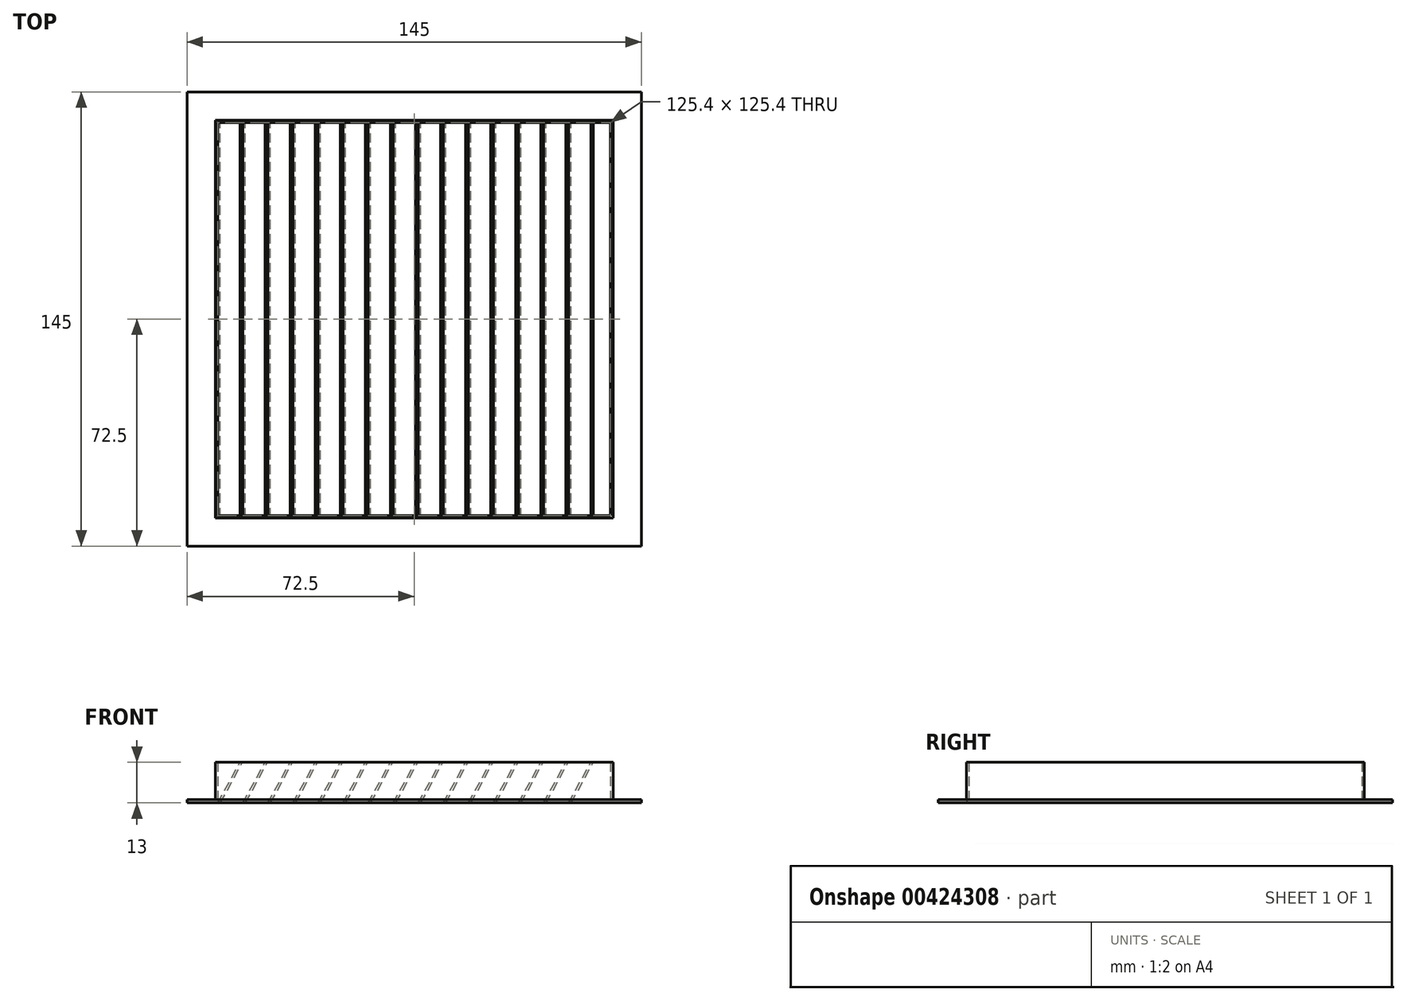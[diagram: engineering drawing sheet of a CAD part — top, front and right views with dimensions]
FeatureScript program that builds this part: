
annotation { "Feature Type Name" : "Feature", "Feature Type Description" : "" }
export const myFeature = defineFeature(function(context is Context, id is Id, definition is map)
    precondition{}
    {
        {
            var Q0;
            Q0=qCreatedBy(makeId("Top.planeOp"),FACE);
            var sketch = newSketch(context, id + "F0", { "sketchPlane" : qUnion([Q0])});
            skLineSegment(sketch, "E0.bottom", {"start": v(63.5, -63.5) * mm, "end": v(-63.5, -63.5) * mm});
            skLineSegment(sketch, "E0.top", {"start": v(63.5, 63.5) * mm, "end": v(-63.5, 63.5) * mm});
            skLineSegment(sketch, "E0.left", {"start": v(63.5, -63.5) * mm, "end": v(63.5, 63.5) * mm});
            skLineSegment(sketch, "E0.right", {"start": v(-63.5, -63.5) * mm, "end": v(-63.5, 63.5) * mm});
            skPoint(sketch, "E0.middle", {"position": v(0, 0) * mm});
            skLineSegment(sketch, "E1.0", {"start": v(62.7, 62.7) * mm, "end": v(-62.7, 62.7) * mm});
            skLineSegment(sketch, "E1.1", {"start": v(62.7, -62.7) * mm, "end": v(62.7, 62.7) * mm});
            skLineSegment(sketch, "E1.2", {"start": v(62.7, -62.7) * mm, "end": v(-62.7, -62.7) * mm});
            skLineSegment(sketch, "E1.3", {"start": v(-62.7, -62.7) * mm, "end": v(-62.7, 62.7) * mm});
            skLineSegment(sketch, "E2.bottom", {"start": v(72.5, -72.5) * mm, "end": v(-72.5, -72.5) * mm});
            skLineSegment(sketch, "E2.top", {"start": v(72.5, 72.5) * mm, "end": v(-72.5, 72.5) * mm});
            skLineSegment(sketch, "E2.left", {"start": v(72.5, -72.5) * mm, "end": v(72.5, 72.5) * mm});
            skLineSegment(sketch, "E2.right", {"start": v(-72.5, -72.5) * mm, "end": v(-72.5, 72.5) * mm});
            skSolve(sketch);
        }
        {
            var Q0;
            Q0=makeQuery(id+"F0.imprint","IMPRINT",FACE,{"disambiguationData":[TD([[makeQuery(id+"F0.imprint","IMPRINT",EDGE,{"derivedFrom":sQuery(id+"F0.wireOp",EDGE,"E0.bottom")}),1.0]])]});
            var Q1;
            Q1=makeQuery(id+"F0.imprint","IMPRINT",FACE,{"disambiguationData":[TD([[makeQuery(id+"F0.imprint","IMPRINT",EDGE,{"derivedFrom":sQuery(id+"F0.wireOp",EDGE,"E0.bottom")}),-1.0]])]});
            extrude(context, id + "F1", {"entities" : qUnion([Q0, Q1]), "depth" : 1 * mm});
        }
        {
            var Q0;
            Q0=makeQuery(id+"F0.imprint","IMPRINT",FACE,{"disambiguationData":[TD([[makeQuery(id+"F0.imprint","IMPRINT",EDGE,{"derivedFrom":sQuery(id+"F0.wireOp",EDGE,"E0.bottom")}),-1.0]])]});
            extrude(context, id + "F2", {"entities" : qUnion([Q0]), "operationType" : NewBodyOperationType.ADD, "depth" : 13 * mm});
        }
        {
            var Q0;
            {var subQ0=sQuery(id+"F0.wireOp",EDGE,"E1.0");Q0=makeQuery(id+"F2.boolean.opBoolean","MERGE",FACE,{"derivedFrom":[makeQuery(id+"F1.opExtrude","SWEPT_FACE",FACE,{"disambiguationData":[OSD([subQ0])]}),makeQuery(id+"F2.opExtrude","SWEPT_FACE",FACE,{"disambiguationData":[OSD([subQ0])]})]});}
            var sketch = newSketch(context, id + "F3", { "sketchPlane" : qUnion([Q0])});
            skLineSegment(sketch, "E3", {"start": v(-62.7, 0) * mm, "end": v(-55.61, 13) * mm});
            skLineSegment(sketch, "E4", {"start": v(-61.9, 0) * mm, "end": v(-54.81, 13) * mm});
            skLineSegment(sketch, "E5.1.0.0", {"start": v(-54.7, 0) * mm, "end": v(-47.61, 13) * mm});
            skLineSegment(sketch, "E5.1.0.1", {"start": v(-53.9, 0) * mm, "end": v(-46.81, 13) * mm});
            skLineSegment(sketch, "E5.2.0.0", {"start": v(-46.7, 0) * mm, "end": v(-39.61, 13) * mm});
            skLineSegment(sketch, "E5.2.0.1", {"start": v(-45.9, 0) * mm, "end": v(-38.81, 13) * mm});
            skLineSegment(sketch, "E5.3.0.0", {"start": v(-38.7, 0) * mm, "end": v(-31.61, 13) * mm});
            skLineSegment(sketch, "E5.3.0.1", {"start": v(-37.9, 0) * mm, "end": v(-30.81, 13) * mm});
            skLineSegment(sketch, "E5.4.0.0", {"start": v(-30.7, 0) * mm, "end": v(-23.61, 13) * mm});
            skLineSegment(sketch, "E5.4.0.1", {"start": v(-29.9, 0) * mm, "end": v(-22.81, 13) * mm});
            skLineSegment(sketch, "E5.5.0.0", {"start": v(-22.7, 0) * mm, "end": v(-15.61, 13) * mm});
            skLineSegment(sketch, "E5.5.0.1", {"start": v(-21.9, 0) * mm, "end": v(-14.81, 13) * mm});
            skLineSegment(sketch, "E5.6.0.0", {"start": v(-14.7, 0) * mm, "end": v(-7.61, 13) * mm});
            skLineSegment(sketch, "E5.6.0.1", {"start": v(-13.9, 0) * mm, "end": v(-6.81, 13) * mm});
            skLineSegment(sketch, "E5.7.0.0", {"start": v(-6.7, 0) * mm, "end": v(0.39, 13) * mm});
            skLineSegment(sketch, "E5.7.0.1", {"start": v(-5.9, 0) * mm, "end": v(1.19, 13) * mm});
            skLineSegment(sketch, "E5.8.0.0", {"start": v(1.3, 0) * mm, "end": v(8.39, 13) * mm});
            skLineSegment(sketch, "E5.8.0.1", {"start": v(2.1, 0) * mm, "end": v(9.19, 13) * mm});
            skLineSegment(sketch, "E5.9.0.0", {"start": v(9.3, 0) * mm, "end": v(16.39, 13) * mm});
            skLineSegment(sketch, "E5.9.0.1", {"start": v(10.1, 0) * mm, "end": v(17.19, 13) * mm});
            skLineSegment(sketch, "E5.10.0.0", {"start": v(17.3, 0) * mm, "end": v(24.39, 13) * mm});
            skLineSegment(sketch, "E5.10.0.1", {"start": v(18.1, 0) * mm, "end": v(25.19, 13) * mm});
            skLineSegment(sketch, "E5.11.0.0", {"start": v(25.3, 0) * mm, "end": v(32.39, 13) * mm});
            skLineSegment(sketch, "E5.11.0.1", {"start": v(26.1, 0) * mm, "end": v(33.19, 13) * mm});
            skLineSegment(sketch, "E5.12.0.0", {"start": v(33.3, 0) * mm, "end": v(40.39, 13) * mm});
            skLineSegment(sketch, "E5.12.0.1", {"start": v(34.1, 0) * mm, "end": v(41.19, 13) * mm});
            skLineSegment(sketch, "E5.13.0.0", {"start": v(41.3, 0) * mm, "end": v(48.39, 13) * mm});
            skLineSegment(sketch, "E5.13.0.1", {"start": v(42.1, 0) * mm, "end": v(49.19, 13) * mm});
            skLineSegment(sketch, "E5.14.0.0", {"start": v(49.3, 0) * mm, "end": v(56.39, 13) * mm});
            skLineSegment(sketch, "E5.14.0.1", {"start": v(50.1, 0) * mm, "end": v(57.19, 13) * mm});
            skLineSegment(sketch, "E5.direction1", {"start": v(-62.7, 0) * mm, "end": v(-54.7, 0) * mm, "construction": true});
            skSolve(sketch);
        }
        {
            var Q0;
            {var subQ0=sQuery(id+"F3.wireOp",EDGE,"E3");Q0=makeQuery(id+"F3.imprint","IMPRINT",FACE,{"disambiguationData":[TD([[makeQuery(id+"F3.imprint","IMPRINT",EDGE,{"derivedFrom":subQ0}),-1.0]])]});}
            var Q1;
            {var subQ0=sQuery(id+"F3.wireOp",EDGE,"E5.1.0.0");Q1=makeQuery(id+"F3.imprint","IMPRINT",FACE,{"disambiguationData":[TD([[makeQuery(id+"F3.imprint","IMPRINT",EDGE,{"derivedFrom":subQ0}),-1.0]])]});}
            var Q2;
            {var subQ0=sQuery(id+"F3.wireOp",EDGE,"E5.2.0.0");Q2=makeQuery(id+"F3.imprint","IMPRINT",FACE,{"disambiguationData":[TD([[makeQuery(id+"F3.imprint","IMPRINT",EDGE,{"derivedFrom":subQ0}),-1.0]])]});}
            var Q3;
            {var subQ0=sQuery(id+"F3.wireOp",EDGE,"E5.3.0.0");Q3=makeQuery(id+"F3.imprint","IMPRINT",FACE,{"disambiguationData":[TD([[makeQuery(id+"F3.imprint","IMPRINT",EDGE,{"derivedFrom":subQ0}),-1.0]])]});}
            var Q4;
            {var subQ0=sQuery(id+"F3.wireOp",EDGE,"E5.4.0.0");Q4=makeQuery(id+"F3.imprint","IMPRINT",FACE,{"disambiguationData":[TD([[makeQuery(id+"F3.imprint","IMPRINT",EDGE,{"derivedFrom":subQ0}),-1.0]])]});}
            var Q5;
            {var subQ0=sQuery(id+"F3.wireOp",EDGE,"E5.5.0.0");Q5=makeQuery(id+"F3.imprint","IMPRINT",FACE,{"disambiguationData":[TD([[makeQuery(id+"F3.imprint","IMPRINT",EDGE,{"derivedFrom":subQ0}),-1.0]])]});}
            var Q6;
            {var subQ0=sQuery(id+"F3.wireOp",EDGE,"E5.6.0.0");Q6=makeQuery(id+"F3.imprint","IMPRINT",FACE,{"disambiguationData":[TD([[makeQuery(id+"F3.imprint","IMPRINT",EDGE,{"derivedFrom":subQ0}),-1.0]])]});}
            var Q7;
            {var subQ0=sQuery(id+"F3.wireOp",EDGE,"E5.7.0.0");Q7=makeQuery(id+"F3.imprint","IMPRINT",FACE,{"disambiguationData":[TD([[makeQuery(id+"F3.imprint","IMPRINT",EDGE,{"derivedFrom":subQ0}),-1.0]])]});}
            var Q8;
            {var subQ0=sQuery(id+"F3.wireOp",EDGE,"E5.8.0.0");Q8=makeQuery(id+"F3.imprint","IMPRINT",FACE,{"disambiguationData":[TD([[makeQuery(id+"F3.imprint","IMPRINT",EDGE,{"derivedFrom":subQ0}),-1.0]])]});}
            var Q9;
            {var subQ0=sQuery(id+"F3.wireOp",EDGE,"E5.9.0.0");Q9=makeQuery(id+"F3.imprint","IMPRINT",FACE,{"disambiguationData":[TD([[makeQuery(id+"F3.imprint","IMPRINT",EDGE,{"derivedFrom":subQ0}),-1.0]])]});}
            var Q10;
            {var subQ0=sQuery(id+"F3.wireOp",EDGE,"E5.10.0.0");Q10=makeQuery(id+"F3.imprint","IMPRINT",FACE,{"disambiguationData":[TD([[makeQuery(id+"F3.imprint","IMPRINT",EDGE,{"derivedFrom":subQ0}),-1.0]])]});}
            var Q11;
            {var subQ0=sQuery(id+"F3.wireOp",EDGE,"E5.11.0.0");Q11=makeQuery(id+"F3.imprint","IMPRINT",FACE,{"disambiguationData":[TD([[makeQuery(id+"F3.imprint","IMPRINT",EDGE,{"derivedFrom":subQ0}),-1.0]])]});}
            var Q12;
            {var subQ0=sQuery(id+"F3.wireOp",EDGE,"E5.12.0.0");Q12=makeQuery(id+"F3.imprint","IMPRINT",FACE,{"disambiguationData":[TD([[makeQuery(id+"F3.imprint","IMPRINT",EDGE,{"derivedFrom":subQ0}),-1.0]])]});}
            var Q13;
            {var subQ0=sQuery(id+"F3.wireOp",EDGE,"E5.13.0.0");Q13=makeQuery(id+"F3.imprint","IMPRINT",FACE,{"disambiguationData":[TD([[makeQuery(id+"F3.imprint","IMPRINT",EDGE,{"derivedFrom":subQ0}),-1.0]])]});}
            var Q14;
            {var subQ0=sQuery(id+"F3.wireOp",EDGE,"E5.14.0.0");Q14=makeQuery(id+"F3.imprint","IMPRINT",FACE,{"disambiguationData":[TD([[makeQuery(id+"F3.imprint","IMPRINT",EDGE,{"derivedFrom":subQ0}),-1.0]])]});}
            var Q15;
            {var subQ0=sQuery(id+"F3.wireOp",EDGE,"524b8a1f-dfb2-4648-83e8-d59a4865afdb.0.15.0");Q15=makeQuery(id+"F3.imprint","IMPRINT",FACE,{"disambiguationData":[TD([[makeQuery(id+"F3.imprint","IMPRINT",EDGE,{"derivedFrom":subQ0}),-1.0]])]});}
            var Q16;
            {var subQ0=sQuery(id+"F3.wireOp",EDGE,"524b8a1f-dfb2-4648-83e8-d59a4865afdb.0.16.0");Q16=makeQuery(id+"F3.imprint","IMPRINT",FACE,{"disambiguationData":[TD([[makeQuery(id+"F3.imprint","IMPRINT",EDGE,{"derivedFrom":subQ0}),-1.0]])]});}
            var Q17;
            {var subQ0=sQuery(id+"F3.wireOp",EDGE,"524b8a1f-dfb2-4648-83e8-d59a4865afdb.0.17.0");Q17=makeQuery(id+"F3.imprint","IMPRINT",FACE,{"disambiguationData":[TD([[makeQuery(id+"F3.imprint","IMPRINT",EDGE,{"derivedFrom":subQ0}),-1.0]])]});}
            var Q18;
            {var subQ0=sQuery(id+"F3.wireOp",EDGE,"c68b673f-466f-4e14-b55f-f1e87c093d1d.0.18.0");Q18=makeQuery(id+"F3.imprint","IMPRINT",FACE,{"disambiguationData":[TD([[makeQuery(id+"F3.imprint","IMPRINT",EDGE,{"derivedFrom":subQ0}),-1.0]])]});}
            var Q19;
            {var subQ0=sQuery(id+"F3.wireOp",EDGE,"97451168-7e2a-43d1-a3cc-25ced06fd7a9.0.19.0");Q19=makeQuery(id+"F3.imprint","IMPRINT",FACE,{"disambiguationData":[TD([[makeQuery(id+"F3.imprint","IMPRINT",EDGE,{"derivedFrom":subQ0}),-1.0]])]});}
            extrude(context, id + "F4", {"entities" : qUnion([Q0, Q1, Q2, Q3, Q4, Q5, Q6, Q7, Q8, Q9, Q10, Q11, Q12, Q13, Q14, Q15, Q16, Q17, Q18, Q19]), "depth" : 126 * mm, "hasSecondDirection" : true, "secondDirectionOppositeDirection" : true, "secondDirectionDepth" : 0.8 * mm});
        }
    });
